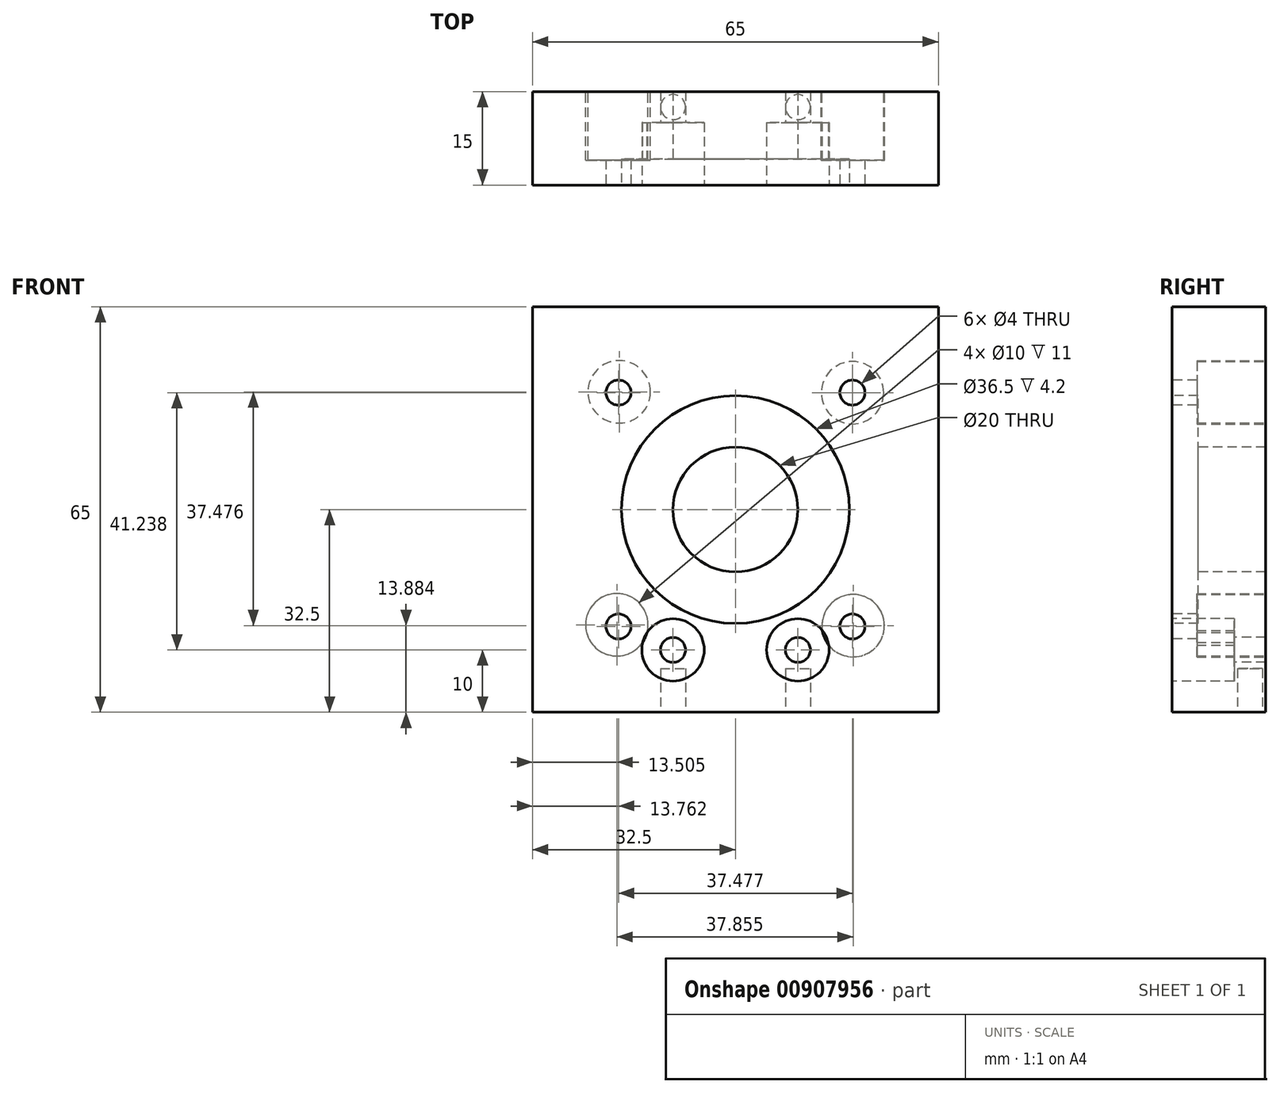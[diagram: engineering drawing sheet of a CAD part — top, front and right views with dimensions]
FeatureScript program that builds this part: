
annotation { "Feature Type Name" : "Feature", "Feature Type Description" : "" }
export const myFeature = defineFeature(function(context is Context, id is Id, definition is map)
    precondition{}
    {
        {
            var Q0;
            Q0=qCreatedBy(makeId("Front.planeOp"),FACE);
            var sketch = newSketch(context, id + "F0", { "sketchPlane" : qUnion([Q0])});
            skLineSegment(sketch, "E0.bottom", {"start": v(32.5, -32.5) * mm, "end": v(-32.5, -32.5) * mm});
            skLineSegment(sketch, "E0.top", {"start": v(32.5, 32.5) * mm, "end": v(-32.5, 32.5) * mm});
            skLineSegment(sketch, "E0.left", {"start": v(32.5, -32.5) * mm, "end": v(32.5, 32.5) * mm});
            skLineSegment(sketch, "E0.right", {"start": v(-32.5, -32.5) * mm, "end": v(-32.5, 32.5) * mm});
            skPoint(sketch, "E0.middle", {"position": v(0, 0) * mm});
            skSolve(sketch);
        }
        {
            var Q0;
            Q0 = qSketchRegion(id + "F0", true);
            extrude(context, id + "F1", {"entities" : qUnion([Q0]), "depth" : 15 * mm, "offsetDistance" : 25 * mm});
        }
        {
            var Q0;
            Q0=makeQuery(id+"F1.opExtrude","CAP_FACE",FACE,{"disambiguationData":[OSD([sQuery(id+"F0.wireOp",EDGE,"E0.bottom"),sQuery(id+"F0.wireOp",EDGE,"E0.top"),sQuery(id+"F0.wireOp",EDGE,"E0.left"),sQuery(id+"F0.wireOp",EDGE,"E0.right")])],"isStart":false});
            var sketch = newSketch(context, id + "F2", { "sketchPlane" : qUnion([Q0])});
            skCircle(sketch, "E1", {"center": v(0, 0) * mm, "radius": 18.25 * mm});
            skSolve(sketch);
        }
        {
            var Q0;
            Q0 = qSketchRegion(id + "F2", true);
            extrude(context, id + "F3", {"entities" : qUnion([Q0]), "operationType" : NewBodyOperationType.REMOVE, "oppositeDirection" : true, "depth" : 4.2 * mm, "offsetDistance" : 25 * mm});
        }
        {
            var Q0;
            Q0=makeQuery(id+"F1.opExtrude","CAP_FACE",FACE,{"disambiguationData":[OSD([sQuery(id+"F0.wireOp",EDGE,"E0.bottom"),sQuery(id+"F0.wireOp",EDGE,"E0.top"),sQuery(id+"F0.wireOp",EDGE,"E0.left"),sQuery(id+"F0.wireOp",EDGE,"E0.right")])],"isStart":false});
            var sketch = newSketch(context, id + "F4", { "sketchPlane" : qUnion([Q0])});
            skCircle(sketch, "E2", {"center": v(0, 0) * mm, "radius": 10 * mm});
            skSolve(sketch);
        }
        {
            var Q0;
            Q0 = qSketchRegion(id + "F4", true);
            extrude(context, id + "F5", {"entities" : qUnion([Q0]), "operationType" : NewBodyOperationType.REMOVE, "oppositeDirection" : true, "depth" : 25 * mm, "offsetDistance" : 25 * mm});
        }
        {
            var Q0;
            Q0=makeQuery(id+"F1.opExtrude","CAP_FACE",FACE,{"disambiguationData":[OSD([sQuery(id+"F0.wireOp",EDGE,"E0.bottom"),sQuery(id+"F0.wireOp",EDGE,"E0.top"),sQuery(id+"F0.wireOp",EDGE,"E0.left"),sQuery(id+"F0.wireOp",EDGE,"E0.right")])],"isStart":false});
            var sketch = newSketch(context, id + "F6", { "sketchPlane" : qUnion([Q0])});
            skLineSegment(sketch, "E3", {"start": v(0, -32.5) * mm, "end": v(0, -22.5) * mm});
            skLineSegment(sketch, "E4", {"start": v(0, -22.5) * mm, "end": v(10, -22.5) * mm});
            skLineSegment(sketch, "E5", {"start": v(0, -22.5) * mm, "end": v(-10, -22.5) * mm});
            skCircle(sketch, "E6", {"center": v(-10, -22.5) * mm, "radius": 5 * mm});
            skPoint(sketch, "E6.perimeterSnap0", {"position": v(0, -27.5) * mm});
            skPoint(sketch, "E6.perimeterSnap1", {"position": v(-5, -22.5) * mm});
            skCircle(sketch, "E7", {"center": v(10, -22.5) * mm, "radius": 5 * mm});
            skSolve(sketch);
        }
        {
            var Q0;
            Q0 = qSketchRegion(id + "F6", true);
            extrude(context, id + "F7", {"entities" : qUnion([Q0]), "operationType" : NewBodyOperationType.REMOVE, "oppositeDirection" : true, "depth" : 10 * mm, "offsetDistance" : 25 * mm});
        }
        {
            var Q0;
            Q0=makeQuery(id+"F1.opExtrude","CAP_FACE",FACE,{"disambiguationData":[OSD([sQuery(id+"F0.wireOp",EDGE,"E0.bottom"),sQuery(id+"F0.wireOp",EDGE,"E0.top"),sQuery(id+"F0.wireOp",EDGE,"E0.left"),sQuery(id+"F0.wireOp",EDGE,"E0.right")])],"isStart":false});
            var sketch = newSketch(context, id + "F8", { "sketchPlane" : qUnion([Q0])});
            skCircle(sketch, "E8", {"center": v(-10, -22.5) * mm, "radius": 2 * mm});
            skCircle(sketch, "E9", {"center": v(10, -22.5) * mm, "radius": 2 * mm});
            skSolve(sketch);
        }
        {
            var Q0;
            Q0 = qSketchRegion(id + "F8", true);
            extrude(context, id + "F9", {"entities" : qUnion([Q0]), "operationType" : NewBodyOperationType.REMOVE, "oppositeDirection" : true, "depth" : 25 * mm, "offsetDistance" : 25 * mm});
        }
        {
            var Q0;
            Q0=makeQuery(id+"F1.opExtrude","CAP_FACE",FACE,{"disambiguationData":[OSD([sQuery(id+"F0.wireOp",EDGE,"E0.bottom"),sQuery(id+"F0.wireOp",EDGE,"E0.top"),sQuery(id+"F0.wireOp",EDGE,"E0.left"),sQuery(id+"F0.wireOp",EDGE,"E0.right")])],"isStart":true});
            var sketch = newSketch(context, id + "F10", { "sketchPlane" : qUnion([Q0])});
            skSolve(sketch);
        }
        {
            var Q0;
            Q0=makeQuery(id+"F1.opExtrude","CAP_FACE",FACE,{"disambiguationData":[OSD([sQuery(id+"F0.wireOp",EDGE,"E0.bottom"),sQuery(id+"F0.wireOp",EDGE,"E0.top"),sQuery(id+"F0.wireOp",EDGE,"E0.left"),sQuery(id+"F0.wireOp",EDGE,"E0.right")])],"isStart":false});
            var sketch = newSketch(context, id + "F11", { "sketchPlane" : qUnion([Q0])});
            skCircle(sketch, "E10", {"center": v(0, 0) * mm, "radius": 26.5 * mm, "construction": true});
            skLineSegment(sketch, "E11", {"start": v(32.5, 32.5) * mm, "end": v(-32.5, -32.5) * mm, "construction": true});
            skLineSegment(sketch, "E12", {"start": v(-32.5, 32.5) * mm, "end": v(32.5, -32.5) * mm, "construction": true});
            skCircle(sketch, "E13", {"center": v(18.74, 18.74) * mm, "radius": 5 * mm});
            skCircle(sketch, "E14", {"center": v(-18.74, 18.74) * mm, "radius": 5 * mm});
            skCircle(sketch, "E15", {"center": v(18.74, -18.74) * mm, "radius": 5 * mm});
            skCircle(sketch, "E16", {"center": v(-18.74, -18.74) * mm, "radius": 5 * mm});
            skCircle(sketch, "E17", {"center": v(-18.74, 18.74) * mm, "radius": 2 * mm});
            skCircle(sketch, "E18", {"center": v(18.74, 18.74) * mm, "radius": 2 * mm});
            skCircle(sketch, "E19", {"center": v(-18.74, -18.74) * mm, "radius": 2 * mm});
            skCircle(sketch, "E20", {"center": v(18.74, -18.74) * mm, "radius": 2 * mm});
            skSolve(sketch);
        }
        {
            var Q0;
            {var subQ3=sQuery(id+"F0.wireOp",EDGE,"E0.bottom");Q0=makeQuery(id+"F10.imprint","IMPRINT",FACE,{"disambiguationData":[TD([[makeQuery(id+"F10.imprint","IMPRINT",EDGE,{"derivedFrom":makeQuery(id+"F1.opExtrude","CAP_EDGE",EDGE,{"disambiguationData":[OSD([subQ3])],"isStart":true})}),1.0]])]});}
            var sketch = newSketch(context, id + "F12", { "sketchPlane" : qUnion([Q0])});
            skCircle(sketch, "E21", {"center": v(0, 0) * mm, "radius": 26.5 * mm, "construction": true});
            skLineSegment(sketch, "E22", {"start": v(32.7, 32.93) * mm, "end": v(-32.7, -32.45) * mm, "construction": true});
            skLineSegment(sketch, "E23", {"start": v(-32.93, 32.7) * mm, "end": v(33.42, -32.7) * mm, "construction": true});
            skCircle(sketch, "E24", {"center": v(18.62, 18.86) * mm, "radius": 5 * mm});
            skCircle(sketch, "E25", {"center": v(19, -18.48) * mm, "radius": 5 * mm});
            skCircle(sketch, "E26", {"center": v(-18.86, -18.62) * mm, "radius": 5 * mm});
            skCircle(sketch, "E27", {"center": v(-18.76, 18.72) * mm, "radius": 5 * mm});
            skSolve(sketch);
        }
        {
            var Q0;
            Q0 = qSketchRegion(id + "F12", true);
            extrude(context, id + "F13", {"entities" : qUnion([Q0]), "operationType" : NewBodyOperationType.REMOVE, "oppositeDirection" : true, "depth" : 11 * mm, "offsetDistance" : 25 * mm});
        }
        {
            var Q0;
            Q0=makeQuery(id+"F11.imprint","IMPRINT",FACE,{"disambiguationData":[TD([[makeQuery(id+"F11.imprint","IMPRINT",EDGE,{"derivedFrom":sQuery(id+"F11.wireOp",EDGE,"E17")}),1.0]])]});
            var Q1;
            Q1=makeQuery(id+"F11.imprint","IMPRINT",FACE,{"disambiguationData":[TD([[makeQuery(id+"F11.imprint","IMPRINT",EDGE,{"derivedFrom":sQuery(id+"F11.wireOp",EDGE,"E19")}),1.0]])]});
            var Q2;
            Q2=makeQuery(id+"F11.imprint","IMPRINT",FACE,{"disambiguationData":[TD([[makeQuery(id+"F11.imprint","IMPRINT",EDGE,{"derivedFrom":sQuery(id+"F11.wireOp",EDGE,"E18")}),1.0]])]});
            var Q3;
            Q3=makeQuery(id+"F11.imprint","IMPRINT",FACE,{"disambiguationData":[TD([[makeQuery(id+"F11.imprint","IMPRINT",EDGE,{"derivedFrom":sQuery(id+"F11.wireOp",EDGE,"E20")}),1.0]])]});
            extrude(context, id + "F14", {"entities" : qUnion([Q0, Q1, Q2, Q3]), "operationType" : NewBodyOperationType.REMOVE, "oppositeDirection" : true, "depth" : 25 * mm, "offsetDistance" : 25 * mm});
        }
        {
            var Q0;
            Q0=makeQuery(id+"F1.opExtrude","SWEPT_FACE",FACE,{"disambiguationData":[OSD([sQuery(id+"F0.wireOp",EDGE,"E0.bottom")])]});
            var sketch = newSketch(context, id + "F15", { "sketchPlane" : qUnion([Q0])});
            skLineSegment(sketch, "E28", {"start": v(0, 0) * mm, "end": v(10, 0) * mm});
            skLineSegment(sketch, "E29", {"start": v(10, 0) * mm, "end": v(10, 2.5) * mm});
            skLineSegment(sketch, "E30", {"start": v(10, 2.5) * mm, "end": v(-10, 2.5) * mm});
            skCircle(sketch, "E31", {"center": v(-10, 2.5) * mm, "radius": 2 * mm});
            skCircle(sketch, "E32", {"center": v(10, 2.5) * mm, "radius": 2 * mm});
            skSolve(sketch);
        }
        {
            var Q0;
            Q0 = qSketchRegion(id + "F15", true);
            extrude(context, id + "F16", {"entities" : qUnion([Q0]), "operationType" : NewBodyOperationType.REMOVE, "oppositeDirection" : true, "depth" : 7 * mm, "offsetDistance" : 25 * mm});
        }
    });
